# Revit family: QF_MACOM_CB06E-DA
name_source: partatom
category: Equipamento especial
units: mm (PartAtom-declared; Revit-internal decimal feet)

## family parameters
Com base no plano de trabalho = Não
Compartilhado = Não
Corte com vazios quando carregada = Não
Cota do conector redondo = Utilizar diâmetro
Número OmniClass = 23.40.40.14.17.11
Ponto de cálculo do ambiente = Não
Sempre na vertical = Sim
Tipo de parte = Normal
Título OmniClass = Cookers, Ovens, Stoves

## types (2) — shared parameters
Depth = 686,000 mm
Descrição = CHAR BROILER EXPORTACAO MACOM 610, DUPLO GAS
Elevação padrão = 0,000 mm
Fabricante = MACOM
Gas Connection Height = 60,000 mm
Gas Size = 3/4"
Height = 395,000 mm
Modelo = CB06E-DA
Number of Burners = 4
Show Clearances = Sim
URL = https://www.acosmacom.com.br
Volume = 0,17 m³
Weight = 49,00 kg
Width = 610,000 mm

## per-type parameters (varying)
| type | Gas Consumption GLP | Gas Consumption GN | Gas Input GLP | Gas Input GN | Gas Pressure |
| CB06E-G | 1,48 Kg/h | 0 m³/h | 67485 Btu/h |  | 0,03 bar |
| CB06E-N |  | 2 m³/h | 0 Btu/h | 17020 Kcal/h | 0,02 bar |

## geometry (parser evidence)
native form markers: Sweep x4
no freeform markers — native parametric forms only
